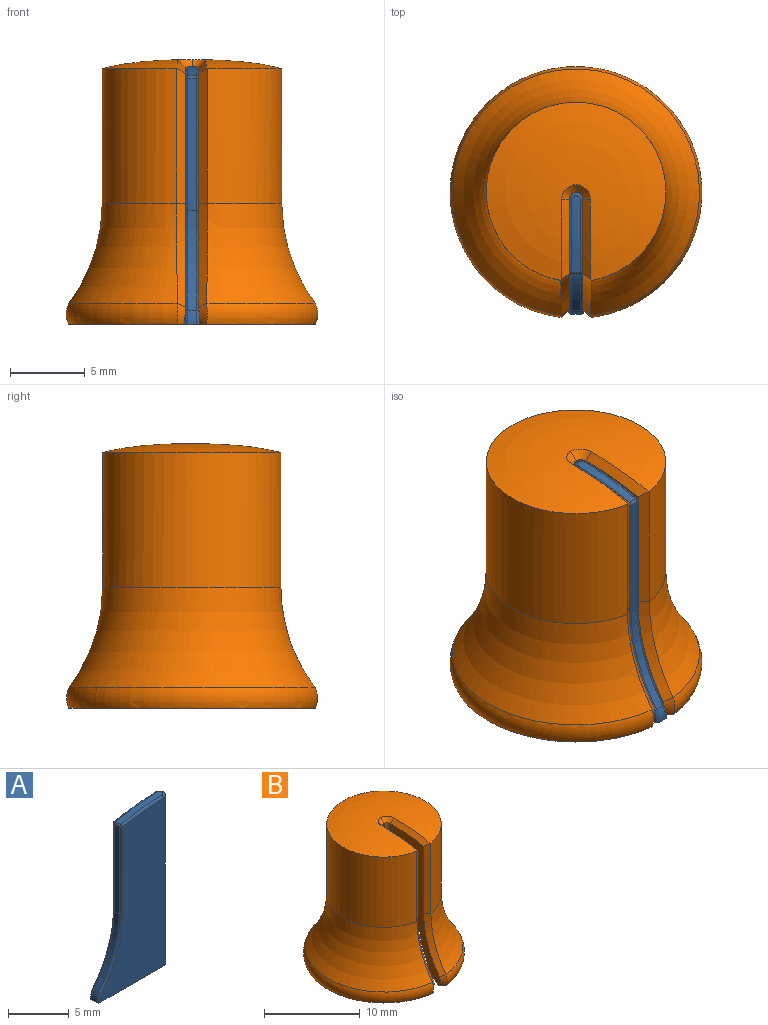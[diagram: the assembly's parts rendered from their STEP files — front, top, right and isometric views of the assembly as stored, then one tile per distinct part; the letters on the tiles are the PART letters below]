
ASSEMBLY  parts=2 mates=1
PART A: 20 faces, bbox 8.8x1x17.2 mm
  f0: plane 8.81x0.6mm, normal (-1,0,0), area 5.3mm2, adj f1,f8,f12,f15
  f1: cylinder r=11.1mm len=6.69mm, axis (0,1,0), area 4.4mm2, adj f0,f2,f10,f13
  f2: cylinder r=1.6mm len=0.91mm, axis (0,1,0), area 0.6mm2, adj f1,f3,f9,f11
  f3: plane 8.15x1.01mm, normal (0,0,-1), area 8mm2, adj f2,f5,f6,f7,f9,f11
  f4: extruded ~5.1x0.6mm, area 3mm2, adj f8,f16,f18,f19
  f5: plane 17x7.45mm, normal (0,-1,0), area 87.7mm2, adj f3,f7,f9,f10,f12,f16
  f6: plane 17x7.45mm, normal (0,1,0), area 87.7mm2, adj f3,f7,f11,f13,f15,f19
  f7: cylinder r=0.5mm len=17.01mm, axis (0,0,-1), area 26.7mm2, adj f3,f5,f6,f18
  f8: cylinder r=0.2mm len=0.6mm, axis (0,1,0), area 0.2mm2, adj f0,f4,f14,f17
  f9: torus R=1.4mm, axis (0,-1,0), area 0.3mm2, adj f2,f3,f5,f10
  f10: torus R=11.3mm, axis (0,-1,0), area 2.3mm2, adj f1,f5,f9,f12
  f11: torus R=1.4mm, axis (0,-1,0), area 0.3mm2, adj f2,f3,f6,f13
  f12: cylinder r=0.2mm len=8.81mm, axis (0,0,1), area 2.8mm2, adj f0,f5,f10,f14
  f13: torus R=11.3mm, axis (0,-1,0), area 2.3mm2, adj f1,f6,f11,f15
  f14: sphere r=0.2mm, area 0.1mm2, adj f8,f12,f16
  f15: cylinder r=0.2mm len=8.81mm, axis (0,0,-1), area 2.8mm2, adj f0,f6,f13,f17
  f16: bspline ~6.25x0.93mm, area 1.5mm2, adj f4,f5,f14,f18
  f17: sphere r=0.2mm, area 0.1mm2, adj f8,f15,f19
  f18: bspline ~1x0.62mm, area 0.4mm2, adj f4,f7,f16,f19
  f19: bspline ~6.25x0.93mm, area 1.5mm2, adj f4,f6,f17,f18
PART B: 39 faces, bbox 20.5x20.4x18.7 mm
  f0: plane 10x9.98mm, normal (0,0,-1), area 46.7mm2, adj f1,f2,f3,f9,f10,f14,f15,f16
  f1: cylinder r=3.02mm len=10.8mm, axis (0,0,-1), area 9.1mm2, adj f0,f10,f11,f24
  f2: cylinder r=3.02mm len=10.8mm, axis (0,0,-1), area 34.9mm2, adj f0,f11,f18,f21
  f3: cylinder r=3.02mm len=10.8mm, axis (0,0,-1), area 34.9mm2, adj f0,f11,f19,f26
  f4: cylinder r=6mm len=12mm, axis (0,0,-1), area 320.7mm2, adj f5,f8,f31,f36
  f5: revolved ~11.96x11.92mm, area 102.4mm2, adj f4,f31,f32,f33,f34,f35,f36
  f6: plane 16.61x16.61mm, normal (0,0,-1), area 36.1mm2, adj f7,f12,f16,f17,f29,f38
  f7: torus R=6.81mm, axis (0,0,-1), area 73.1mm2, adj f6,f8,f29,f38
  f8: torus R=17.1mm, axis (0,0,-1), area 291.4mm2, adj f4,f7,f30,f37
  f9: cylinder r=5mm len=10mm, axis (0,0,-1), area 30.5mm2, adj f0,f13,f16,f17
  f10: plane 10.8x2.16mm, normal (0,1,0), area 23.4mm2, adj f0,f1,f11,f16
  f11: plane 8.45x5.75mm, normal (0,0,-1), area 27.5mm2, adj f1,f2,f3,f10,f14,f15,f16,f17
  f12: cone r=5mm half-angle=45deg, axis (0,0,-1), area 65.8mm2, adj f6,f13,f16,f17
  f13: cone r=5mm half-angle=22.5deg, axis (0,0,-1), area 129.2mm2, adj f9,f12,f16,f17
  f14: cylinder r=3.02mm len=10.8mm, axis (0,0,-1), area 9.1mm2, adj f0,f11,f15,f23
  f15: plane 10.8x2.16mm, normal (0,1,0), area 23.4mm2, adj f0,f11,f14,f17
  f16: plane 17.72x7.91mm, normal (1,0,0), area 51.5mm2, adj f0,f6,f9,f10,f11,f12,f13,f27
  f17: plane 17.72x7.9mm, normal (-1,0,0), area 51.5mm2, adj f0,f6,f9,f11,f12,f13,f15,f28
  f18: plane 10.8x1.29mm, normal (-1,0,0), area 14mm2, adj f0,f2,f11,f20
  f19: plane 10.8x1.29mm, normal (1,0,0), area 14mm2, adj f0,f3,f11,f20
  f20: plane 10.8x1.5mm, normal (0,-1,0), area 16.2mm2, adj f0,f11,f18,f19
  f21: plane 10.8x1.29mm, normal (0,-1,0), area 14mm2, adj f0,f2,f11,f22
  f22: plane 10.8x1.5mm, normal (-1,0,0), area 16.2mm2, adj f0,f11,f21,f23
  f23: plane 10.8x1.29mm, normal (0,1,0), area 14mm2, adj f0,f11,f14,f22
  f24: plane 10.8x1.29mm, normal (0,1,0), area 14mm2, adj f0,f1,f11,f25
  f25: plane 10.8x1.5mm, normal (1,0,0), area 16.2mm2, adj f0,f11,f24,f26
  f26: plane 10.8x1.29mm, normal (0,-1,0), area 14mm2, adj f0,f3,f11,f25
  f27: cylinder r=0.5mm len=0.9mm, axis (0,0,1), area 0.7mm2, adj f11,f16,f28,f34
  f28: cylinder r=0.5mm len=0.9mm, axis (0,0,-1), area 0.7mm2, adj f11,f17,f27,f33
  f29: bspline ~1.71x0.74mm, area 1mm2, adj f6,f7,f17,f30
  f30: bspline ~7.32x3.02mm, area 5.5mm2, adj f8,f17,f29,f31
  f31: plane 9.02x0.58mm, normal (-0.64,-0.77,0), area 6.7mm2, adj f4,f5,f17,f30,f32
  f32: bspline ~5.76x1.15mm, area 3.7mm2, adj f5,f17,f31,f33
  f33: bspline ~1.01x0.98mm, area 0.8mm2, adj f5,f28,f32,f34
  f34: bspline ~1.05x1.04mm, area 0.8mm2, adj f5,f27,f33,f35
  f35: bspline ~5.71x1.13mm, area 3.7mm2, adj f5,f16,f34,f36
  f36: plane 9.02x0.58mm, normal (0.64,-0.77,0), area 6.7mm2, adj f4,f5,f16,f35,f37
  f37: bspline ~7.32x3.02mm, area 5.5mm2, adj f8,f16,f36,f38
  f38: bspline ~1.71x0.74mm, area 1mm2, adj f6,f7,f16,f37
PLACE A rot(axis=(0,0,1),90deg) t=(-63.36,109.1,-1.63)mm
PLACE B t=(-62.86,-3.2,39.44)mm
MATE planar B.f6 <-> A.f3  axis (0,0,-1) through (-61.86,-11.39,34.76)mm
